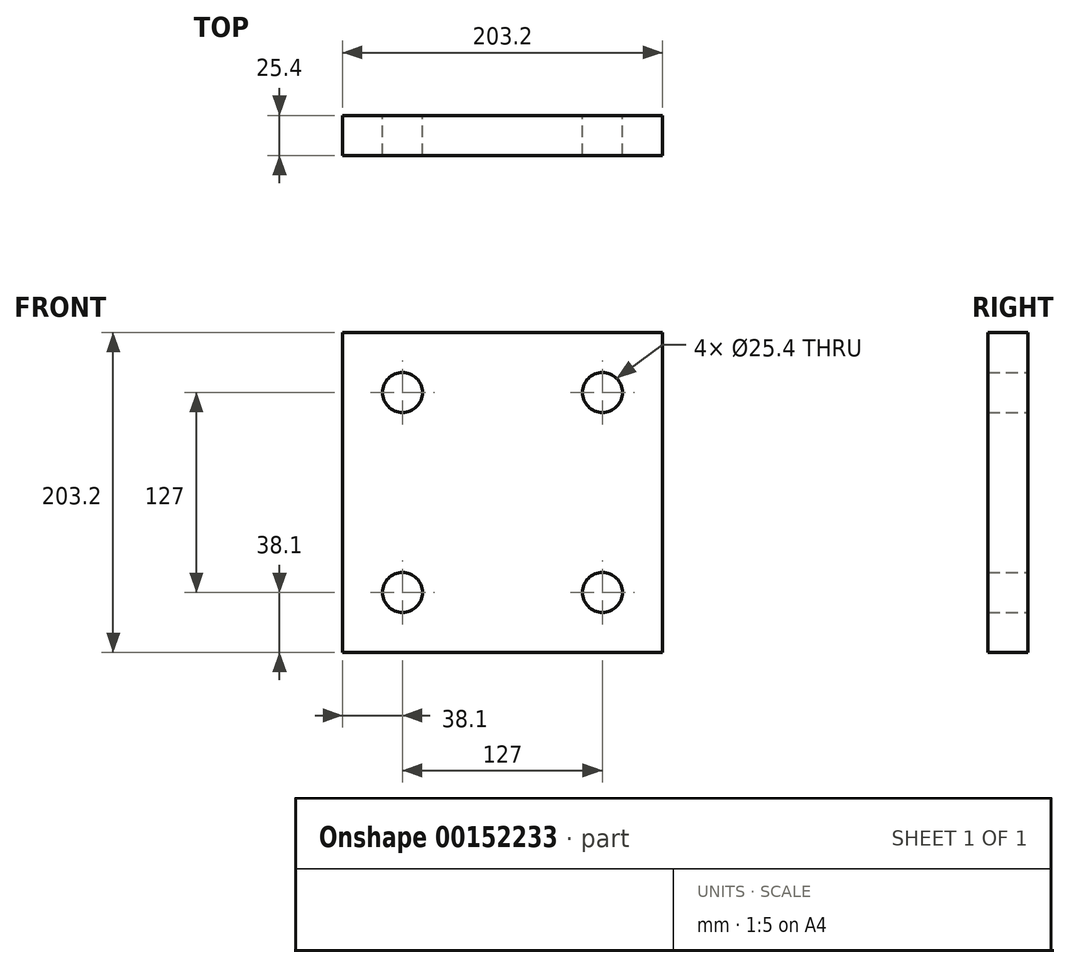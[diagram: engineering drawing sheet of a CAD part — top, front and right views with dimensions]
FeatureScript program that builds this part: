
annotation { "Feature Type Name" : "Feature", "Feature Type Description" : "" }
export const myFeature = defineFeature(function(context is Context, id is Id, definition is map)
    precondition{}
    {
        {
            var Q0;
            Q0=qCreatedBy(makeId("Front.planeOp"),FACE);
            var sketch = newSketch(context, id + "F0", { "sketchPlane" : qUnion([Q0])});
            skCircle(sketch, "E0", {"center": v(-63.5, 63.5) * mm, "radius": 12.7 * mm});
            skCircle(sketch, "E1", {"center": v(63.5, 63.5) * mm, "radius": 12.7 * mm});
            skCircle(sketch, "E2", {"center": v(63.5, -63.5) * mm, "radius": 12.7 * mm});
            skCircle(sketch, "E3", {"center": v(-63.5, -63.5) * mm, "radius": 12.7 * mm});
            skLineSegment(sketch, "E4", {"start": v(-63.5, -63.5) * mm, "end": v(-63.5, 63.5) * mm, "construction": true});
            skLineSegment(sketch, "E5", {"start": v(-63.5, 63.5) * mm, "end": v(63.5, 63.5) * mm, "construction": true});
            skLineSegment(sketch, "E6", {"start": v(63.5, 63.5) * mm, "end": v(63.5, -63.5) * mm, "construction": true});
            skLineSegment(sketch, "E7", {"start": v(-63.5, -63.5) * mm, "end": v(63.5, -63.5) * mm, "construction": true});
            skLineSegment(sketch, "E8", {"start": v(0, 63.5) * mm, "end": v(0, 0) * mm, "construction": true});
            skLineSegment(sketch, "E9", {"start": v(-63.5, 0) * mm, "end": v(0, 0) * mm, "construction": true});
            skLineSegment(sketch, "E10.bottom", {"start": v(-101.6, 101.6) * mm, "end": v(101.6, 101.6) * mm});
            skLineSegment(sketch, "E10.top", {"start": v(-101.6, -101.6) * mm, "end": v(101.6, -101.6) * mm});
            skLineSegment(sketch, "E10.left", {"start": v(-101.6, 101.6) * mm, "end": v(-101.6, -101.6) * mm});
            skLineSegment(sketch, "E10.right", {"start": v(101.6, 101.6) * mm, "end": v(101.6, -101.6) * mm});
            skPoint(sketch, "E10.middle", {"position": v(0, 0) * mm});
            skSolve(sketch);
        }
        {
            var Q0;
            Q0=makeQuery(id+"F0.imprint","IMPRINT",FACE,{"disambiguationData":[TD([[makeQuery(id+"F0.imprint","IMPRINT",EDGE,{"derivedFrom":sQuery(id+"F0.wireOp",EDGE,"E0")}),-1.0]])]});
            extrude(context, id + "F1", {"entities" : qUnion([Q0]), "depth" : 25.4 * mm});
        }
    });
